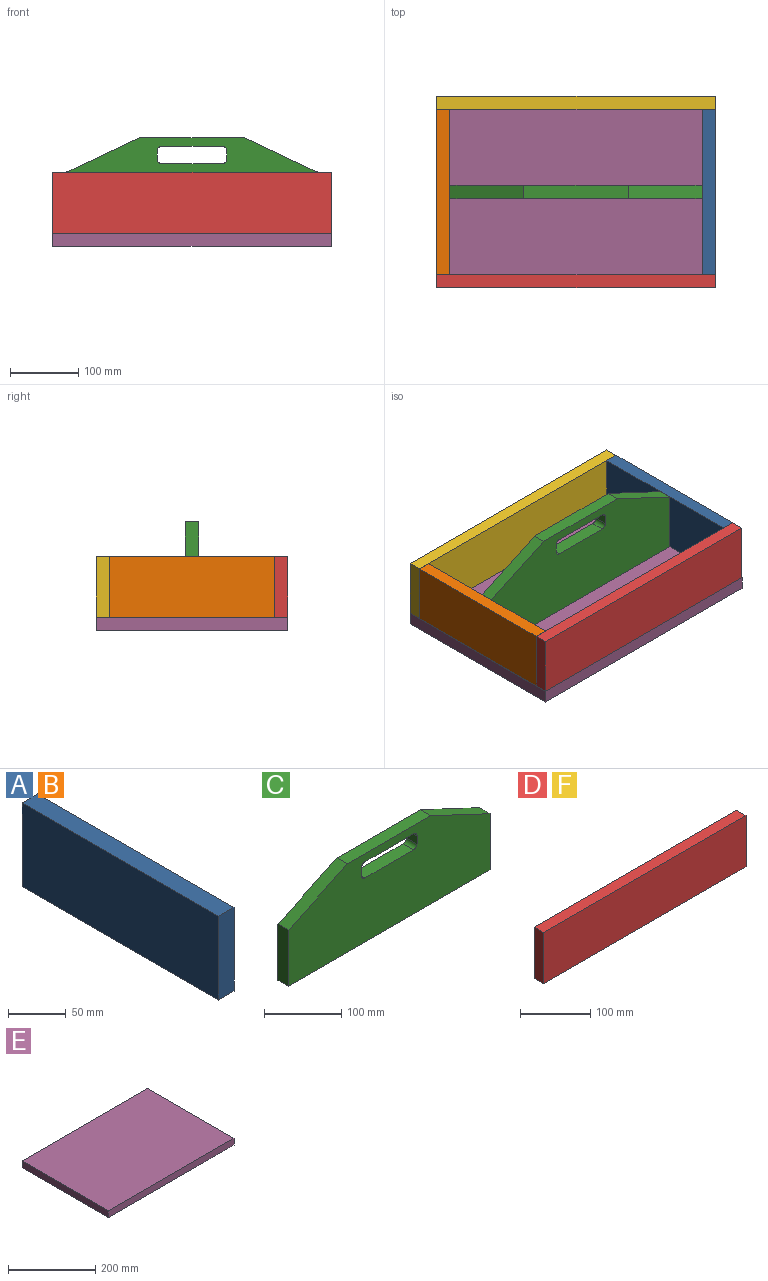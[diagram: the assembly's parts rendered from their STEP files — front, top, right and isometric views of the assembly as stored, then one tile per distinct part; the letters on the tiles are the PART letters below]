
ASSEMBLY  parts=6 mates=5
PART A: 6 faces, bbox 19.1x241.3x89 mm
  f0: plane 241.3x19.05mm, normal (0,0,1), area 4596.8mm2, adj f1,f3,f4,f5
  f1: plane 89x19.05mm, normal (0,-1,0), area 1695.5mm2, adj f0,f2,f4,f5
  f2: plane 241.3x19.05mm, normal (0,0,-1), area 4596.8mm2, adj f1,f3,f4,f5
  f3: plane 89x19.05mm, normal (0,1,0), area 1695.5mm2, adj f0,f2,f4,f5
  f4: plane 241.3x89mm, normal (1,0,0), area 21476.5mm2, adj f0,f1,f2,f3
  f5: plane 241.3x89mm, normal (-1,0,0), area 21476.5mm2, adj f0,f1,f2,f3
PART B: same geometry as A
PART C: 16 faces, bbox 368.3x19.1x139.7 mm
  f0: plane 88.9x19.05mm, normal (0,0,1), area 1693.5mm2, adj f1,f13,f14,f15
  f1: cylinder r=6.35mm len=19.05mm, axis (0,1,0), area 190mm2, adj f0,f2,f14,f15
  f2: plane 19.05x12.7mm, normal (1,0,0), area 241.9mm2, adj f1,f3,f14,f15
  f3: cylinder r=6.35mm len=19.05mm, axis (0,1,0), area 190mm2, adj f2,f4,f14,f15
  f4: plane 88.9x19.05mm, normal (0,0,-1), area 1693.5mm2, adj f3,f5,f14,f15
  f5: cylinder r=6.35mm len=19.05mm, axis (0,1,0), area 190mm2, adj f4,f6,f14,f15
  f6: plane 19.05x12.7mm, normal (-1,0,0), area 241.9mm2, adj f5,f13,f14,f15
  f7: plane 152.4x19.05mm, normal (0,0,1), area 2903.2mm2, adj f8,f12,f14,f15
  f8: plane 107.95x50.8mm, normal (-0.43,0,0.9), area 2272.8mm2, adj f7,f9,f14,f15
  f9: plane 88.9x19.05mm, normal (-1,0,0), area 1693.5mm2, adj f8,f10,f14,f15
  f10: plane 368.3x19.05mm, normal (0,0,-1), area 7016.1mm2, adj f9,f11,f14,f15
  f11: plane 88.9x19.05mm, normal (1,0,0), area 1693.5mm2, adj f10,f12,f14,f15
  f12: plane 107.95x50.8mm, normal (0.43,0,0.9), area 2272.8mm2, adj f7,f11,f14,f15
  f13: cylinder r=6.35mm len=19.05mm, axis (0,1,0), area 190mm2, adj f0,f6,f14,f15
  f14: plane 368.3x139.7mm, normal (0,-1,0), area 43421.7mm2, adj f0,f1,f2,f3,f4,f5,f6,f7
  f15: plane 368.3x139.7mm, normal (0,1,0), area 43421.7mm2, adj f0,f1,f2,f3,f4,f5,f6,f7
PART D: 6 faces, bbox 406.4x19.1x88.9 mm
  f0: plane 406.4x19.05mm, normal (0,0,1), area 7741.9mm2, adj f1,f3,f4,f5
  f1: plane 88.9x19.05mm, normal (-1,0,0), area 1693.5mm2, adj f0,f2,f4,f5
  f2: plane 406.4x19.05mm, normal (0,0,-1), area 7741.9mm2, adj f1,f3,f4,f5
  f3: plane 88.9x19.05mm, normal (1,0,0), area 1693.5mm2, adj f0,f2,f4,f5
  f4: plane 406.4x88.9mm, normal (0,-1,0), area 36129mm2, adj f0,f1,f2,f3
  f5: plane 406.4x88.9mm, normal (0,1,0), area 36129mm2, adj f0,f1,f2,f3
PART E: 6 faces, bbox 406.4x279.4x19.1 mm
  f0: plane 406.4x19.05mm, normal (0,1,0), area 7741.9mm2, adj f1,f3,f4,f5
  f1: plane 279.4x19.05mm, normal (-1,0,0), area 5322.6mm2, adj f0,f2,f4,f5
  f2: plane 406.4x19.05mm, normal (0,-1,0), area 7741.9mm2, adj f1,f3,f4,f5
  f3: plane 279.4x19.05mm, normal (1,0,0), area 5322.6mm2, adj f0,f2,f4,f5
  f4: plane 406.4x279.4mm, normal (0,0,1), area 113548.2mm2, adj f0,f1,f2,f3
  f5: plane 406.4x279.4mm, normal (0,0,-1), area 113548.2mm2, adj f0,f1,f2,f3
PART F: same geometry as D
PLACE A t=(117.99,-106.77,58.88)mm
PLACE B t=(-269.36,-106.77,58.88)mm
PLACE C t=(-66.16,-27.3,100.49)mm
PLACE D t=(-61.36,-157.47,116.1)mm
PLACE E t=(-65.39,-39.35,-7.46)mm
PLACE F t=(-61.36,102.88,116.1)mm
MATE planar B.f2 <-> D.f2  axis (0,0,1) through (-269.36,-157.47,11.59)mm
MATE planar F.f2 <-> E.f4  axis (0,0,1) through (137.04,102.88,11.59)mm
MATE planar D.f2 <-> E.f4  axis (0,0,1) through (137.04,-176.52,11.59)mm
MATE planar A.f2 <-> D.f2  axis (0,0,1) through (137.04,-157.47,11.59)mm
MATE planar C.f10 <-> E.f4  axis (0,0,-1) through (-66.16,-36.82,11.59)mm
